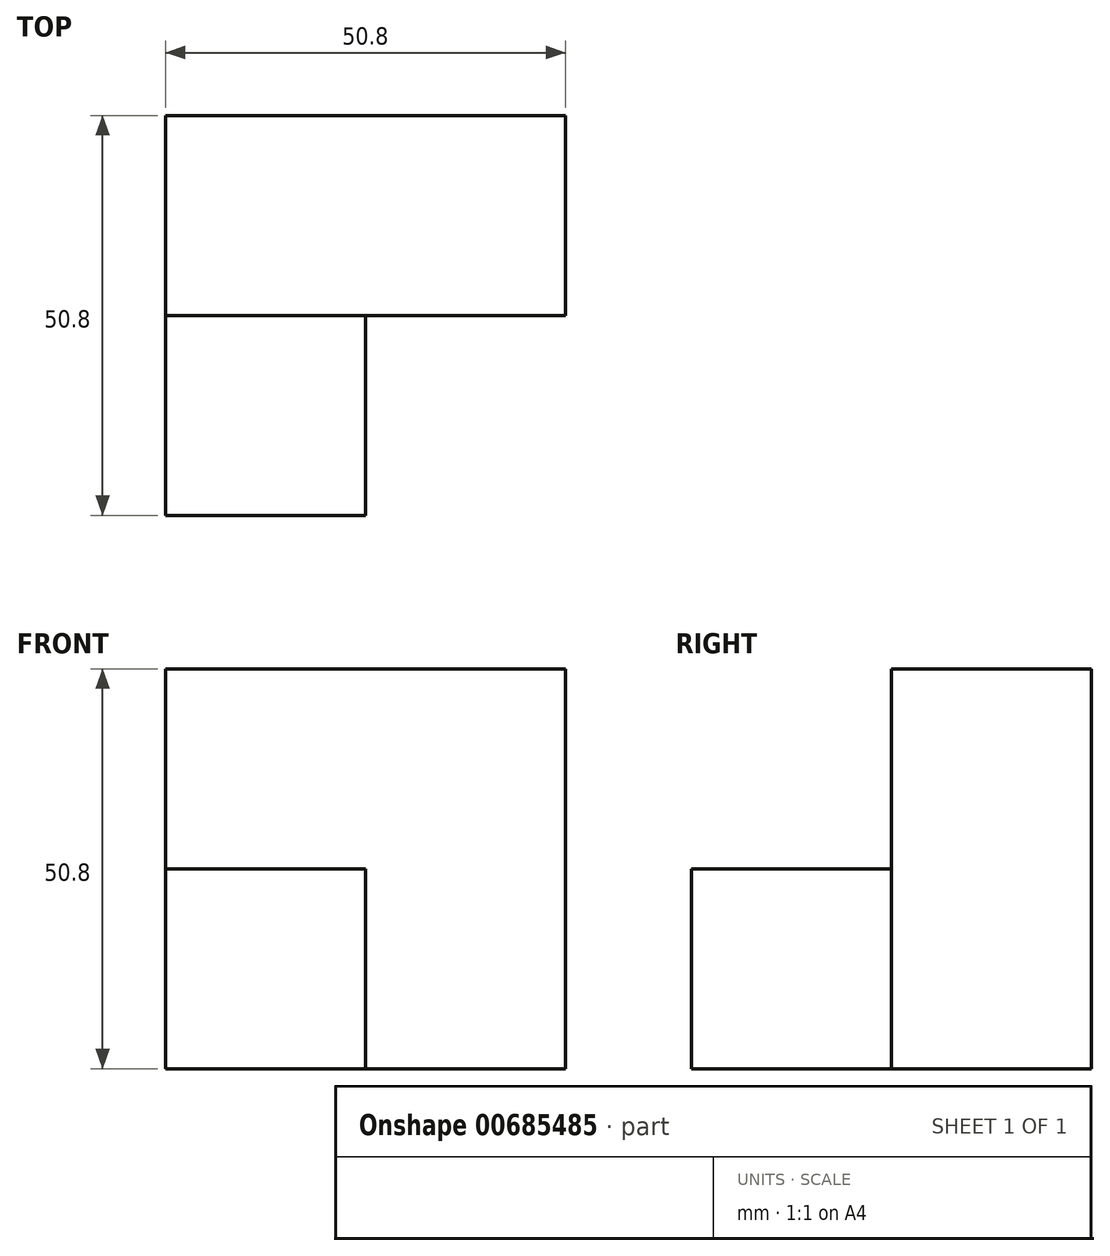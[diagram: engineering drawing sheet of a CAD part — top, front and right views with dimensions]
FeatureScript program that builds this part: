
annotation { "Feature Type Name" : "Feature", "Feature Type Description" : "" }
export const myFeature = defineFeature(function(context is Context, id is Id, definition is map)
    precondition{}
    {
        {
            var Q0;
            Q0=qCreatedBy(makeId("Front.planeOp"),FACE);
            var sketch = newSketch(context, id + "F0", { "sketchPlane" : qUnion([Q0])});
            skLineSegment(sketch, "E0.bottom", {"start": v(-75.83, 43.7) * mm, "end": v(-25.03, 43.7) * mm});
            skLineSegment(sketch, "E0.top", {"start": v(-75.83, -7.1) * mm, "end": v(-25.03, -7.1) * mm});
            skLineSegment(sketch, "E0.left", {"start": v(-75.83, 43.7) * mm, "end": v(-75.83, -7.1) * mm});
            skLineSegment(sketch, "E0.right", {"start": v(-25.03, 43.7) * mm, "end": v(-25.03, -7.1) * mm});
            skLineSegment(sketch, "E1.bottom", {"start": v(-75.83, -7.1) * mm, "end": v(-50.43, -7.1) * mm});
            skLineSegment(sketch, "E1.top", {"start": v(-75.83, 18.3) * mm, "end": v(-50.43, 18.3) * mm});
            skLineSegment(sketch, "E1.left", {"start": v(-75.83, -7.1) * mm, "end": v(-75.83, 18.3) * mm});
            skLineSegment(sketch, "E1.right", {"start": v(-50.43, -7.1) * mm, "end": v(-50.43, 18.3) * mm});
            skSolve(sketch);
        }
        {
            var Q0;
            Q0 = qSketchRegion(id + "F0", true);
            extrude(context, id + "F1", {"entities" : qUnion([Q0]), "depth" : 25.4 * mm, "offsetDistance" : 25.4 * mm});
        }
        {
            var Q0;
            Q0=makeQuery(id+"F1.opExtrude","CAP_FACE",FACE,{"disambiguationData":[OSD([sQuery(id+"F0.wireOp",EDGE,"E0.bottom"),sQuery(id+"F0.wireOp",EDGE,"E0.top"),sQuery(id+"F0.wireOp",EDGE,"E0.left"),sQuery(id+"F0.wireOp",EDGE,"E0.right"),sQuery(id+"F0.wireOp",EDGE,"E1.bottom"),sQuery(id+"F0.wireOp",EDGE,"E1.left")])],"isStart":false});
            var sketch = newSketch(context, id + "F2", { "sketchPlane" : qUnion([Q0])});
            skLineSegment(sketch, "E2.bottom", {"start": v(-75.83, -7.1) * mm, "end": v(-50.43, -7.1) * mm});
            skLineSegment(sketch, "E2.top", {"start": v(-75.83, 18.3) * mm, "end": v(-50.43, 18.3) * mm});
            skLineSegment(sketch, "E2.left", {"start": v(-75.83, -7.1) * mm, "end": v(-75.83, 18.3) * mm});
            skLineSegment(sketch, "E2.right", {"start": v(-50.43, -7.1) * mm, "end": v(-50.43, 18.3) * mm});
            skSolve(sketch);
        }
        {
            var Q0;
            Q0 = qSketchRegion(id + "F2", true);
            extrude(context, id + "F3", {"entities" : qUnion([Q0]), "operationType" : NewBodyOperationType.ADD, "depth" : 25.4 * mm, "offsetDistance" : 25.4 * mm});
        }
    });
